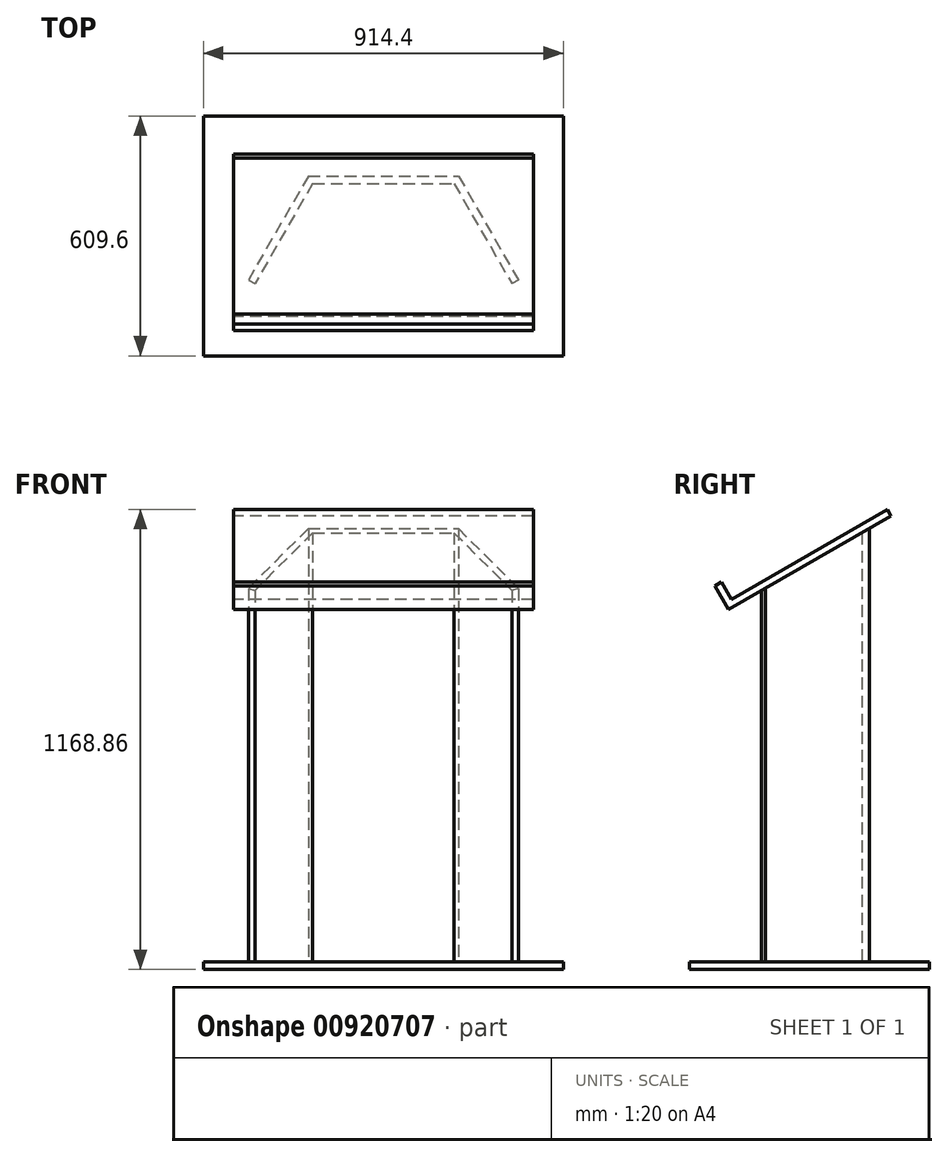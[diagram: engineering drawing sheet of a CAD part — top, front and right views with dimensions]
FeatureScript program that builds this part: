
annotation { "Feature Type Name" : "Feature", "Feature Type Description" : "" }
export const myFeature = defineFeature(function(context is Context, id is Id, definition is map)
    precondition{}
    {
        {
            var Q0;
            Q0=qCreatedBy(makeId("Top.planeOp"),FACE);
            var sketch = newSketch(context, id + "F0", { "sketchPlane" : qUnion([Q0])});
            skLineSegment(sketch, "E0.bottom", {"start": v(457.2, -304.8) * mm, "end": v(-457.2, -304.8) * mm});
            skLineSegment(sketch, "E0.top", {"start": v(457.2, 304.8) * mm, "end": v(-457.2, 304.8) * mm});
            skLineSegment(sketch, "E0.left", {"start": v(457.2, -304.8) * mm, "end": v(457.2, 304.8) * mm});
            skLineSegment(sketch, "E0.right", {"start": v(-457.2, -304.8) * mm, "end": v(-457.2, 304.8) * mm});
            skPoint(sketch, "E0.middle", {"position": v(0, 0) * mm});
            skLineSegment(sketch, "E1", {"start": v(0, 304.8) * mm, "end": v(0, -304.8) * mm, "construction": true});
            skLineSegment(sketch, "E2", {"start": v(-190.5, 152.4) * mm, "end": v(190.5, 152.4) * mm});
            skLineSegment(sketch, "E3", {"start": v(190.5, 152.4) * mm, "end": v(342.9, -111.56) * mm});
            skLineSegment(sketch, "E4", {"start": v(-190.5, 152.4) * mm, "end": v(-342.9, -111.56) * mm});
            skPoint(sketch, "E5", {"position": v(0, 152.4) * mm});
            skLineSegment(sketch, "E6.0", {"start": v(-179.5, 133.35) * mm, "end": v(-326.4, -121.09) * mm});
            skLineSegment(sketch, "E6.1", {"start": v(-179.5, 133.35) * mm, "end": v(179.5, 133.35) * mm});
            skLineSegment(sketch, "E6.2", {"start": v(179.5, 133.35) * mm, "end": v(326.4, -121.09) * mm});
            skLineSegment(sketch, "E7", {"start": v(-342.9, -111.56) * mm, "end": v(-326.4, -121.09) * mm});
            skLineSegment(sketch, "E8", {"start": v(342.9, -111.56) * mm, "end": v(326.4, -121.09) * mm});
            skSolve(sketch);
        }
        {
            var Q0;
            Q0=qCreatedBy(makeId("Right.planeOp"),FACE);
            var sketch = newSketch(context, id + "F1", { "sketchPlane" : qUnion([Q0])});
            skLineSegment(sketch, "E9", {"start": v(-223.37, 984.25) * mm, "end": v(-197.97, 940.26) * mm});
            skLineSegment(sketch, "E10", {"start": v(-197.97, 940.26) * mm, "end": v(197.97, 1168.86) * mm});
            skLineSegment(sketch, "E11", {"start": v(0, 1054.56) * mm, "end": v(0, 0) * mm, "construction": true});
            skLineSegment(sketch, "E12.0", {"start": v(-204.95, 914.23) * mm, "end": v(207.5, 1152.36) * mm});
            skLineSegment(sketch, "E12.1", {"start": v(-239.87, 974.73) * mm, "end": v(-204.95, 914.23) * mm});
            skLineSegment(sketch, "E13", {"start": v(-239.87, 974.73) * mm, "end": v(-223.37, 984.25) * mm});
            skLineSegment(sketch, "E14", {"start": v(197.97, 1168.86) * mm, "end": v(207.5, 1152.36) * mm});
            skSolve(sketch);
        }
        {
            var Q0;
            Q0=makeQuery(id+"F1.imprint","IMPRINT",FACE,{"disambiguationData":[TD([[makeQuery(id+"F1.imprint","IMPRINT",EDGE,{"derivedFrom":sQuery(id+"F1.wireOp",EDGE,"E9")}),-1.0]])]});
            extrude(context, id + "F2", {"entities" : qUnion([Q0]), "endBound" : BoundingType.SYMMETRIC, "depth" : 762 * mm, "offsetDistance" : 25.4 * mm});
        }
        {
            var Q0;
            Q0=makeQuery(id+"F0.imprint","IMPRINT",FACE,{"disambiguationData":[TD([[makeQuery(id+"F0.imprint","IMPRINT",EDGE,{"derivedFrom":sQuery(id+"F0.wireOp",EDGE,"E0.bottom")}),-1.0]])]});
            var Q1;
            Q1=makeQuery(id+"F0.imprint","IMPRINT",FACE,{"disambiguationData":[TD([[makeQuery(id+"F0.imprint","IMPRINT",EDGE,{"derivedFrom":sQuery(id+"F0.wireOp",EDGE,"E2")}),-1.0]])]});
            extrude(context, id + "F3", {"entities" : qUnion([Q0, Q1]), "operationType" : NewBodyOperationType.ADD, "depth" : 19.05 * mm, "offsetDistance" : 25.4 * mm});
        }
        {
            var Q0;
            Q0=makeQuery(id+"F0.imprint","IMPRINT",FACE,{"disambiguationData":[TD([[makeQuery(id+"F0.imprint","IMPRINT",EDGE,{"derivedFrom":sQuery(id+"F0.wireOp",EDGE,"E2")}),-1.0]])]});
            var Q1;
            Q1=makeQuery(id+"F2.opExtrude","SWEPT_FACE",FACE,{"disambiguationData":[OSD([sQuery(id+"F1.wireOp",EDGE,"E12.0")])]});
            extrude(context, id + "F4", {"entities" : qUnion([Q0]), "operationType" : NewBodyOperationType.ADD, "endBound" : BoundingType.UP_TO_SURFACE, "depth" : 25.4 * mm, "endBoundEntityFace" : qUnion([Q1]), "offsetDistance" : 25.4 * mm});
        }
    });
